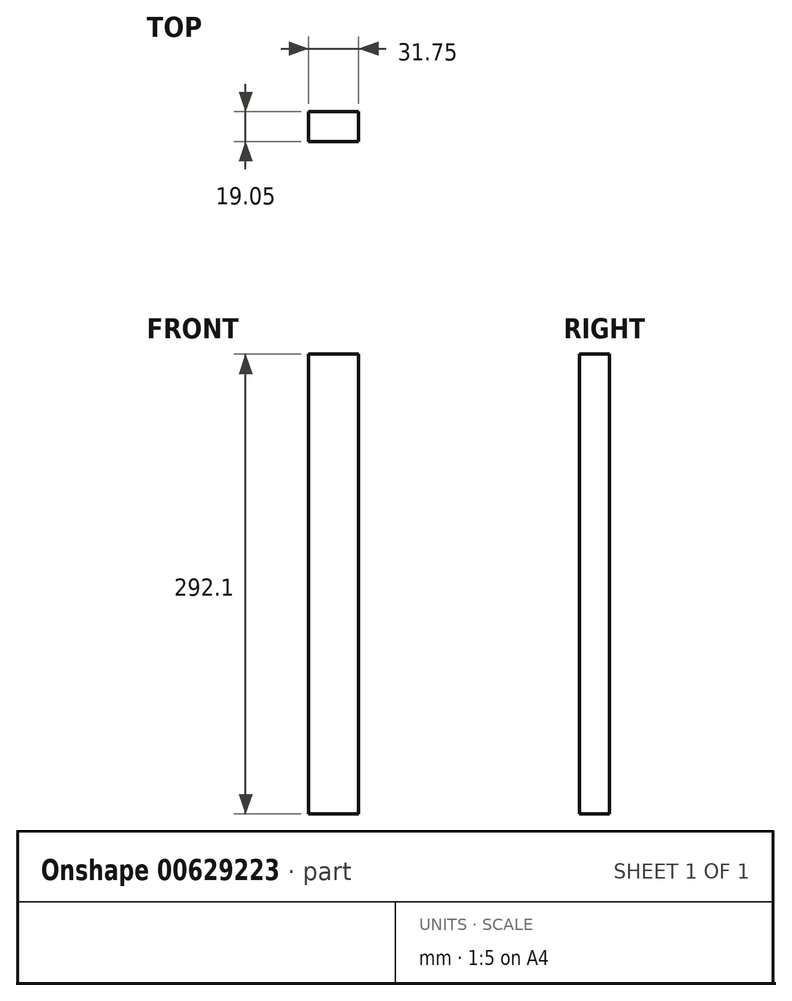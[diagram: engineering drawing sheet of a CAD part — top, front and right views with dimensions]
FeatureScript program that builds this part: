
annotation { "Feature Type Name" : "Feature", "Feature Type Description" : "" }
export const myFeature = defineFeature(function(context is Context, id is Id, definition is map)
    precondition{}
    {
        {
            var Q0;
            Q0=qCreatedBy(makeId("Top.planeOp"),FACE);
            var sketch = newSketch(context, id + "F0", { "sketchPlane" : qUnion([Q0])});
            skLineSegment(sketch, "E0.bottom", {"start": v(0, 0) * mm, "end": v(-31.75, 0) * mm});
            skLineSegment(sketch, "E0.top", {"start": v(0, 19.05) * mm, "end": v(-31.75, 19.05) * mm});
            skLineSegment(sketch, "E0.left", {"start": v(0, 0) * mm, "end": v(0, 19.05) * mm});
            skLineSegment(sketch, "E0.right", {"start": v(-31.75, 0) * mm, "end": v(-31.75, 19.05) * mm});
            skSolve(sketch);
        }
        {
            var Q0;
            Q0=makeQuery(id+"F0.imprint","IMPRINT",FACE,{"disambiguationData":[TD([[makeQuery(id+"F0.imprint","IMPRINT",EDGE,{"derivedFrom":sQuery(id+"F0.wireOp",EDGE,"E0.bottom")}),-1.0]])]});
            extrude(context, id + "F1", {"entities" : qUnion([Q0]), "oppositeDirection" : true, "depth" : 292.1 * mm, "offsetDistance" : 25.4 * mm});
        }
    });
